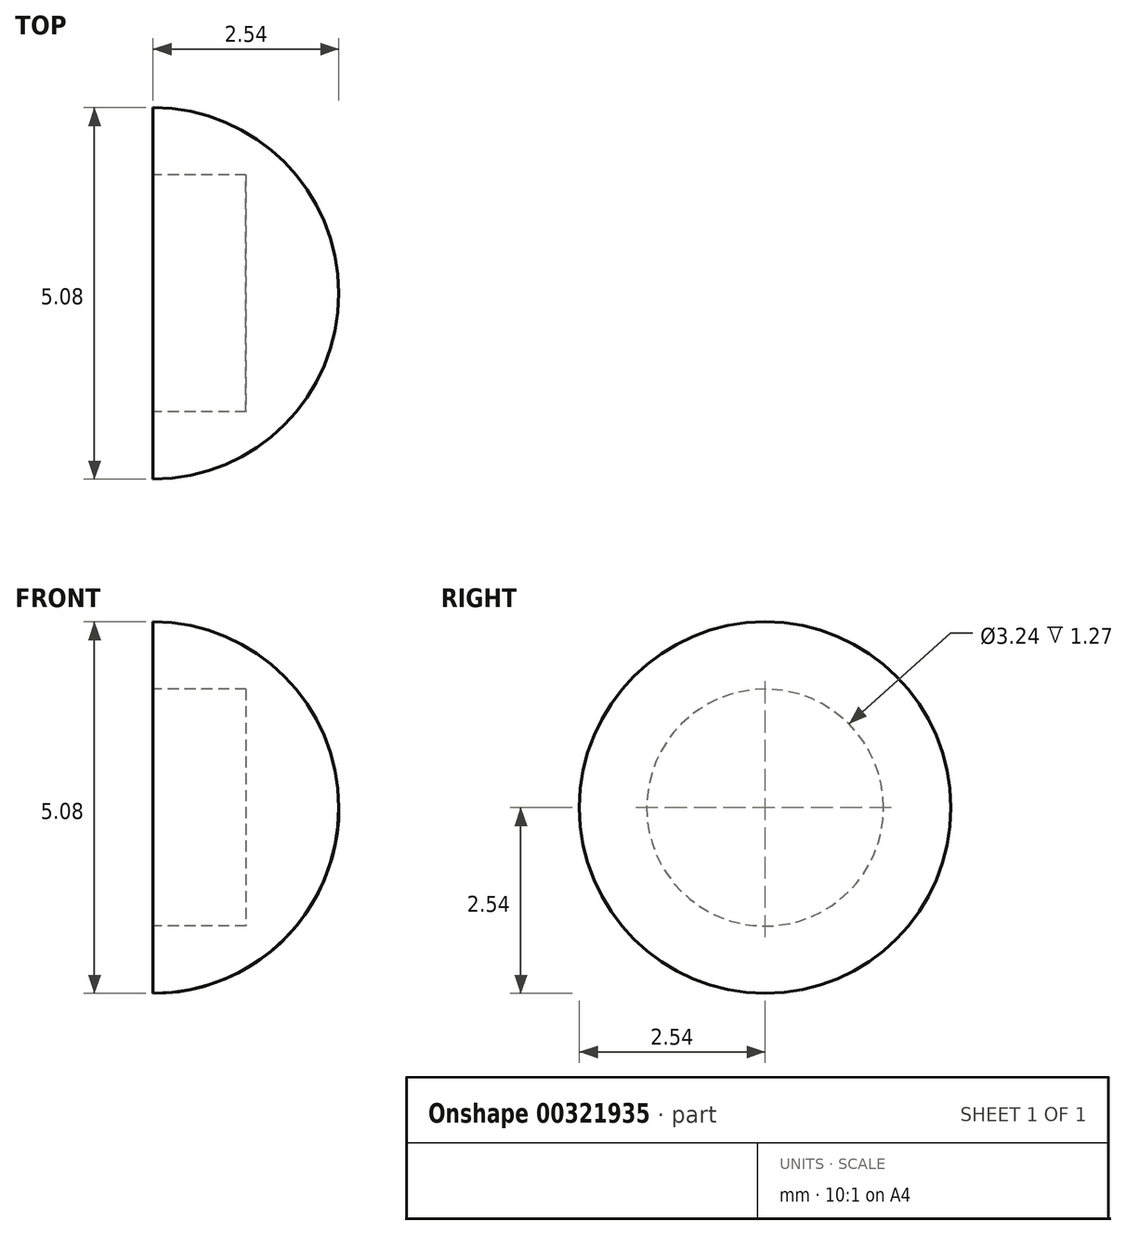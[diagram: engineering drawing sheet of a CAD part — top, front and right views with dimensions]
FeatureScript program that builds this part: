
annotation { "Feature Type Name" : "Feature", "Feature Type Description" : "" }
export const myFeature = defineFeature(function(context is Context, id is Id, definition is map)
    precondition{}
    {
        {
            var Q0;
            Q0=qCreatedBy(makeId("Front.planeOp"),FACE);
            var sketch = newSketch(context, id + "F0", { "sketchPlane" : qUnion([Q0])});
            skArc(sketch, "E0", {"start": v(30.48, 0) * mm, "mid": v(29.74, 1.8) * mm, "end": v(27.94, 2.54) * mm});
            skLineSegment(sketch, "E1", {"start": v(29.21, 0) * mm, "end": v(30.48, 0) * mm});
            skLineSegment(sketch, "E2", {"start": v(27.94, 1.62) * mm, "end": v(27.94, 2.54) * mm});
            skLineSegment(sketch, "E3", {"start": v(27.94, 1.62) * mm, "end": v(29.21, 1.62) * mm});
            skLineSegment(sketch, "E4", {"start": v(29.21, 1.62) * mm, "end": v(29.21, 0) * mm});
            skSolve(sketch);
        }
        {
            var Q0;
            Q0=qSketchRegion(id+"F0",true);
            var Q1;
            Q1=sQuery(id+"F0.wireOp",EDGE,"E1");
            revolve(context, id + "F1", {"entities" : qUnion([Q0]), "axis" : qUnion([Q1]), "revolveType" : RevolveType.FULL});
        }
    });
